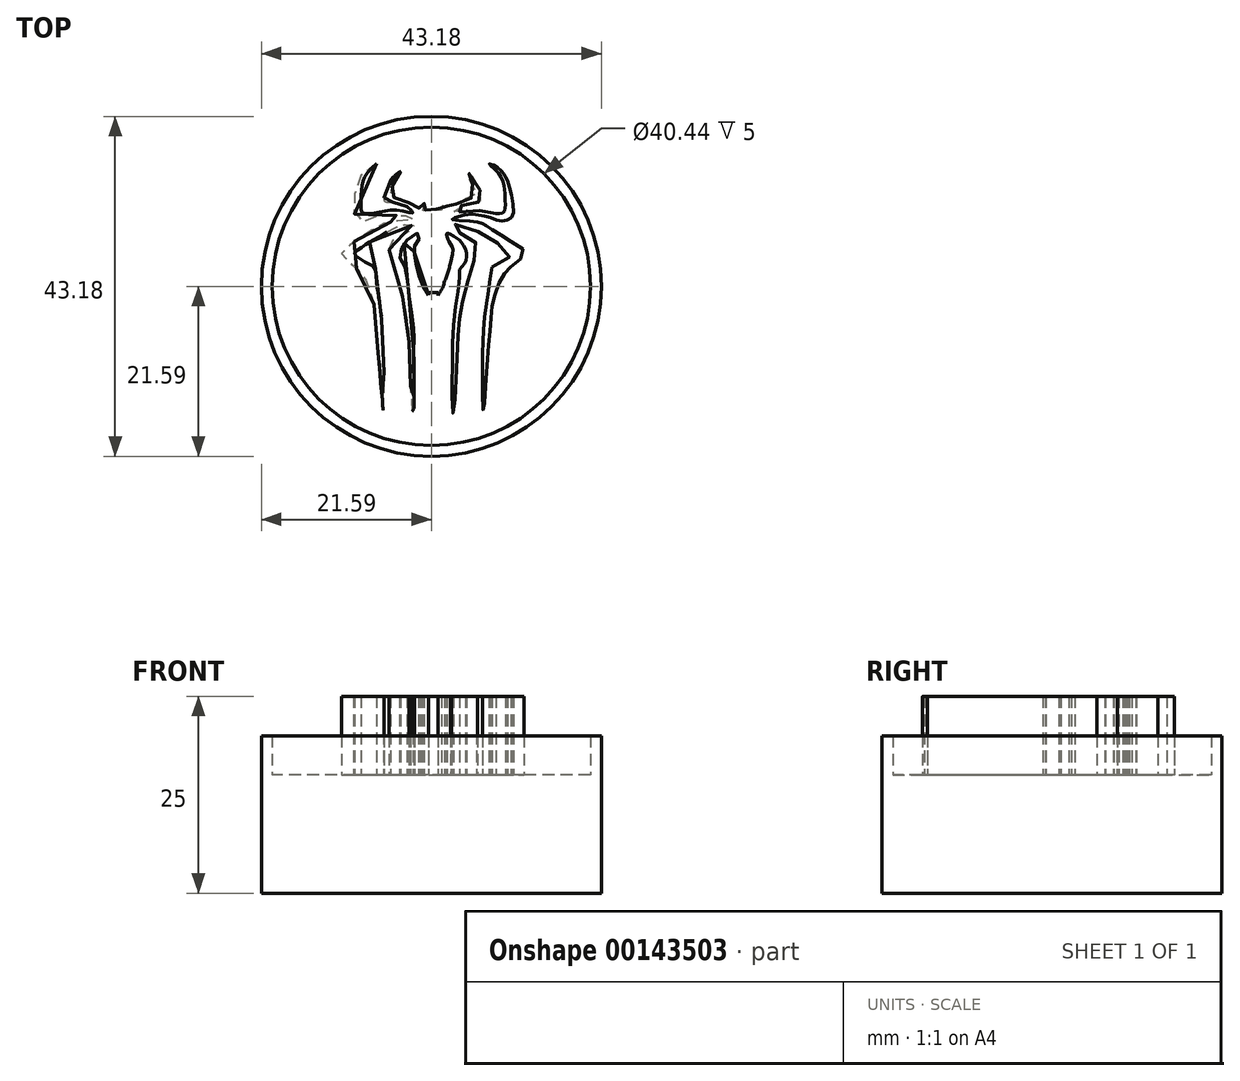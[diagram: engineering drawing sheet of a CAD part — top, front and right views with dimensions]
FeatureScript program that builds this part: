
annotation { "Feature Type Name" : "Feature", "Feature Type Description" : "" }
export const myFeature = defineFeature(function(context is Context, id is Id, definition is map)
    precondition{}
    {
        {
            var Q0;
            Q0=qCreatedBy(makeId("Top.planeOp"),FACE);
            var sketch = newSketch(context, id + "F0", { "sketchPlane" : qUnion([Q0])});
            skCircle(sketch, "E0", {"center": v(0, 0) * mm, "radius": 21.6 * mm});
            skCircle(sketch, "E1", {"center": v(0, 0) * mm, "radius": 20.22 * mm});
            skSolve(sketch);
        }
        {
            var Q0;
            Q0=makeQuery(id+"F0.imprint","IMPRINT",FACE,{"disambiguationData":[TD([[makeQuery(id+"F0.imprint","IMPRINT",EDGE,{"derivedFrom":sQuery(id+"F0.wireOp",EDGE,"E0")}),1.0]])]});
            extrude(context, id + "F1", {"entities" : qUnion([Q0]), "depth" : 20 * mm});
        }
        {
            var Q0;
            Q0=makeQuery(id+"F0.imprint","IMPRINT",FACE,{"disambiguationData":[TD([[makeQuery(id+"F0.imprint","IMPRINT",EDGE,{"derivedFrom":sQuery(id+"F0.wireOp",EDGE,"E1")}),1.0]])]});
            extrude(context, id + "F2", {"entities" : qUnion([Q0]), "operationType" : NewBodyOperationType.ADD, "depth" : 15 * mm});
        }
        {
            var Q0;
            Q0=makeQuery(id+"F2.opExtrude","CAP_FACE",FACE,{"disambiguationData":[OSD([sQuery(id+"F0.wireOp",EDGE,"E1")])],"isStart":false});
            var sketch = newSketch(context, id + "F3", { "sketchPlane" : qUnion([Q0])});
            skPoint(sketch, "E2", {"position": v(-8.55, 14.56) * mm});
            skPoint(sketch, "E3", {"position": v(-9.43, 12.92) * mm});
            skPoint(sketch, "E4", {"position": v(-9.83, 11.06) * mm});
            skPoint(sketch, "E5", {"position": v(-9.83, 9.64) * mm});
            skPoint(sketch, "E6", {"position": v(-9.48, 8.54) * mm});
            skPoint(sketch, "E7", {"position": v(-8.32, 8.54) * mm});
            skPoint(sketch, "E8", {"position": v(-7.4, 8.76) * mm});
            skPoint(sketch, "E9", {"position": v(-6.24, 9.02) * mm});
            skPoint(sketch, "E10", {"position": v(-5.18, 9.02) * mm});
            skPoint(sketch, "E11", {"position": v(-4.25, 9.02) * mm});
            skPoint(sketch, "E12", {"position": v(-3.36, 9.02) * mm});
            skPoint(sketch, "E13", {"position": v(-2.57, 8.67) * mm});
            skPoint(sketch, "E14", {"position": v(-2.18, 8.51) * mm});
            skPoint(sketch, "E15", {"position": v(-3.33, 8.51) * mm});
            skPoint(sketch, "E16", {"position": v(-4.3, 8.3) * mm});
            skPoint(sketch, "E17", {"position": v(-5.35, 8.12) * mm});
            skPoint(sketch, "E18", {"position": v(-6.07, 7.91) * mm});
            skPoint(sketch, "E19", {"position": v(-6.95, 7.47) * mm});
            skPoint(sketch, "E20", {"position": v(-7.67, 7.02) * mm});
            skPoint(sketch, "E21", {"position": v(-8.38, 6.6) * mm});
            skPoint(sketch, "E22", {"position": v(-8.94, 6.22) * mm});
            skPoint(sketch, "E23", {"position": v(-9.8, 5.65) * mm});
            skPoint(sketch, "E24", {"position": v(-10.71, 5.04) * mm});
            skPoint(sketch, "E25", {"position": v(-11.32, 4.59) * mm});
            skPoint(sketch, "E26", {"position": v(-11.32, 3.97) * mm});
            skPoint(sketch, "E27", {"position": v(-10.98, 3.63) * mm});
            skPoint(sketch, "E28", {"position": v(-10.51, 3.17) * mm});
            skPoint(sketch, "E29", {"position": v(-9.87, 2.64) * mm});
            skPoint(sketch, "E30", {"position": v(-9.23, 2.02) * mm});
            skPoint(sketch, "E31", {"position": v(-8.6, 1.38) * mm});
            skPoint(sketch, "E32", {"position": v(-8.23, 0.62) * mm});
            skPoint(sketch, "E33", {"position": v(-7.97, 0) * mm});
            skPoint(sketch, "E34", {"position": v(-7.66, -1.02) * mm});
            skPoint(sketch, "E35", {"position": v(-7.5, -1.48) * mm});
            skPoint(sketch, "E36", {"position": v(-7.26, -2.43) * mm});
            skPoint(sketch, "E37", {"position": v(-7.1, -3.32) * mm});
            skPoint(sketch, "E38", {"position": v(-7.08, -4.27) * mm});
            skPoint(sketch, "E39", {"position": v(-7.04, -4.98) * mm});
            skPoint(sketch, "E40", {"position": v(-6.95, -5.8) * mm});
            skPoint(sketch, "E41", {"position": v(-6.9, -6.93) * mm});
            skPoint(sketch, "E42", {"position": v(-6.8, -7.9) * mm});
            skPoint(sketch, "E43", {"position": v(-6.67, -9.14) * mm});
            skPoint(sketch, "E44", {"position": v(-6.57, -10.22) * mm});
            skPoint(sketch, "E45", {"position": v(-6.5, -11.18) * mm});
            skPoint(sketch, "E46", {"position": v(-6.4, -12.61) * mm});
            skPoint(sketch, "E47", {"position": v(-6.27, -13.83) * mm});
            skPoint(sketch, "E48", {"position": v(-6.17, -15.03) * mm});
            skPoint(sketch, "E49", {"position": v(-6.13, -15.83) * mm});
            skPoint(sketch, "E50", {"position": v(-6.03, -14.04) * mm});
            skPoint(sketch, "E51", {"position": v(-6.01, -12.26) * mm});
            skPoint(sketch, "E52", {"position": v(-6.03, -10.64) * mm});
            skPoint(sketch, "E53", {"position": v(-6.03, -8.76) * mm});
            skPoint(sketch, "E54", {"position": v(-6.03, -7.36) * mm});
            skPoint(sketch, "E55", {"position": v(-6.13, -5.97) * mm});
            skPoint(sketch, "E56", {"position": v(-6.2, -4.96) * mm});
            skPoint(sketch, "E57", {"position": v(-6.34, -3.93) * mm});
            skPoint(sketch, "E58", {"position": v(-6.5, -2.66) * mm});
            skPoint(sketch, "E59", {"position": v(-6.67, -1.54) * mm});
            skPoint(sketch, "E60", {"position": v(-6.8, -0.48) * mm});
            skPoint(sketch, "E61", {"position": v(-7, 0.83) * mm});
            skPoint(sketch, "E62", {"position": v(-7.23, 2.43) * mm});
            skPoint(sketch, "E63", {"position": v(-8.05, 2.9) * mm});
            skPoint(sketch, "E64", {"position": v(-9.08, 3.53) * mm});
            skPoint(sketch, "E65", {"position": v(-9.76, 4.14) * mm});
            skPoint(sketch, "E66", {"position": v(-9.1, 4.78) * mm});
            skPoint(sketch, "E67", {"position": v(-8.22, 5.39) * mm});
            skPoint(sketch, "E68", {"position": v(-7.16, 6.02) * mm});
            skPoint(sketch, "E69", {"position": v(-6.08, 6.63) * mm});
            skPoint(sketch, "E70", {"position": v(-5.26, 7.12) * mm});
            skPoint(sketch, "E71", {"position": v(-4.4, 7.57) * mm});
            skPoint(sketch, "E72", {"position": v(-3.36, 7.83) * mm});
            skPoint(sketch, "E73", {"position": v(-2.42, 7.73) * mm});
            skPoint(sketch, "E74", {"position": v(-2.12, 7.69) * mm});
            skPoint(sketch, "E75", {"position": v(-2.77, 7.05) * mm});
            skPoint(sketch, "E76", {"position": v(-3.71, 6.4) * mm});
            skPoint(sketch, "E77", {"position": v(-4.32, 6.16) * mm});
            skPoint(sketch, "E78", {"position": v(-5.05, 5.72) * mm});
            skPoint(sketch, "E79", {"position": v(-5.33, 4.94) * mm});
            skPoint(sketch, "E80", {"position": v(-5.28, 3.96) * mm});
            skPoint(sketch, "E81", {"position": v(-4.77, 2.6) * mm});
            skPoint(sketch, "E82", {"position": v(-4.37, 1.4) * mm});
            skPoint(sketch, "E83", {"position": v(-4.09, 0.2) * mm});
            skPoint(sketch, "E84", {"position": v(-3.76, -0.76) * mm});
            skPoint(sketch, "E85", {"position": v(-3.55, -1.89) * mm});
            skPoint(sketch, "E86", {"position": v(-3.31, -3.13) * mm});
            skPoint(sketch, "E87", {"position": v(-3.1, -4.4) * mm});
            skPoint(sketch, "E88", {"position": v(-2.98, -5.08) * mm});
            skPoint(sketch, "E89", {"position": v(-2.91, -5.9) * mm});
            skPoint(sketch, "E90", {"position": v(-2.87, -6.96) * mm});
            skPoint(sketch, "E91", {"position": v(-2.82, -8.22) * mm});
            skPoint(sketch, "E92", {"position": v(-2.82, -9.33) * mm});
            skPoint(sketch, "E93", {"position": v(-2.75, -10.26) * mm});
            skPoint(sketch, "E94", {"position": v(-2.7, -11.16) * mm});
            skPoint(sketch, "E95", {"position": v(-2.65, -11.88) * mm});
            skPoint(sketch, "E96", {"position": v(-2.65, -12.78) * mm});
            skPoint(sketch, "E97", {"position": v(-2.56, -13.97) * mm});
            skPoint(sketch, "E98", {"position": v(-2.5, -14.7) * mm});
            skPoint(sketch, "E99", {"position": v(-2.44, -15.76) * mm});
            skPoint(sketch, "E100", {"position": v(-2.33, -16.22) * mm});
            skPoint(sketch, "E101", {"position": v(-2.2, -15.03) * mm});
            skPoint(sketch, "E102", {"position": v(-2.2, -13.6) * mm});
            skPoint(sketch, "E103", {"position": v(-2.19, -12.4) * mm});
            skPoint(sketch, "E104", {"position": v(-2.16, -11.16) * mm});
            skPoint(sketch, "E105", {"position": v(-2.2, -10.36) * mm});
            skPoint(sketch, "E106", {"position": v(-2.23, -9.42) * mm});
            skPoint(sketch, "E107", {"position": v(-2.26, -8.41) * mm});
            skPoint(sketch, "E108", {"position": v(2.77, -16.44) * mm});
            skPoint(sketch, "E109", {"position": v(6.6, -15.83) * mm});
            skPoint(sketch, "E110", {"position": v(2.72, -15.43) * mm});
            skPoint(sketch, "E111", {"position": v(2.65, -14.42) * mm});
            skPoint(sketch, "E112", {"position": v(2.6, -13.46) * mm});
            skPoint(sketch, "E113", {"position": v(2.6, -12.45) * mm});
            skPoint(sketch, "E114", {"position": v(2.62, -11.72) * mm});
            skPoint(sketch, "E115", {"position": v(2.67, -10.83) * mm});
            skPoint(sketch, "E116", {"position": v(2.7, -8.83) * mm});
            skPoint(sketch, "E117", {"position": v(2.67, -6.8) * mm});
            skPoint(sketch, "E118", {"position": v(2.77, -5.38) * mm});
            skPoint(sketch, "E119", {"position": v(3.4, -6.65) * mm});
            skPoint(sketch, "E120", {"position": v(3.28, -8.95) * mm});
            skPoint(sketch, "E121", {"position": v(3.23, -10.66) * mm});
            skPoint(sketch, "E122", {"position": v(3.07, -12.94) * mm});
            skPoint(sketch, "E123", {"position": v(3, -14.37) * mm});
            skPoint(sketch, "E124", {"position": v(-2.2, -6.82) * mm});
            skPoint(sketch, "E125", {"position": v(-2.2, -5.97) * mm});
            skPoint(sketch, "E126", {"position": v(-2.37, -4.42) * mm});
            skPoint(sketch, "E127", {"position": v(-2.7, -1.89) * mm});
            skPoint(sketch, "E128", {"position": v(-3, 0.2) * mm});
            skPoint(sketch, "E129", {"position": v(-3.17, 2.19) * mm});
            skPoint(sketch, "E130", {"position": v(-3.82, 3.02) * mm});
            skPoint(sketch, "E131", {"position": v(-4.01, 3.96) * mm});
            skPoint(sketch, "E132", {"position": v(-3.78, 4.85) * mm});
            skPoint(sketch, "E133", {"position": v(-3.33, 5.65) * mm});
            skPoint(sketch, "E134", {"position": v(-2.58, 6.28) * mm});
            skPoint(sketch, "E135", {"position": v(-1.52, 6.77) * mm});
            skPoint(sketch, "E136", {"position": v(-1.52, 6.11) * mm});
            skPoint(sketch, "E137", {"position": v(-1.76, 5.74) * mm});
            skPoint(sketch, "E138", {"position": v(-2.11, 5.13) * mm});
            skPoint(sketch, "E139", {"position": v(-2.25, 4.8) * mm});
            skPoint(sketch, "E140", {"position": v(-2.09, 3.72) * mm});
            skPoint(sketch, "E141", {"position": v(-1.88, 2.5) * mm});
            skPoint(sketch, "E142", {"position": v(-1.67, 1.66) * mm});
            skPoint(sketch, "E143", {"position": v(-1.27, 0.65) * mm});
            skPoint(sketch, "E144", {"position": v(-0.84, -0.36) * mm});
            skPoint(sketch, "E145", {"position": v(-0.37, -1.14) * mm});
            skPoint(sketch, "E146", {"position": v(0.82, -1.16) * mm});
            skPoint(sketch, "E147", {"position": v(0.82, -0.8) * mm});
            skPoint(sketch, "E148", {"position": v(-0.37, -0.76) * mm});
            skPoint(sketch, "E149", {"position": v(1.36, -0.3) * mm});
            skPoint(sketch, "E150", {"position": v(1.71, 0.7) * mm});
            skPoint(sketch, "E151", {"position": v(2.14, 1.82) * mm});
            skPoint(sketch, "E152", {"position": v(2.42, 2.92) * mm});
            skPoint(sketch, "E153", {"position": v(2.72, 4.82) * mm});
            skPoint(sketch, "E154", {"position": v(2.28, 5.6) * mm});
            skPoint(sketch, "E155", {"position": v(2.04, 6.18) * mm});
            skPoint(sketch, "E156", {"position": v(1.93, 6.72) * mm});
            skPoint(sketch, "E157", {"position": v(2.74, 6.44) * mm});
            skPoint(sketch, "E158", {"position": v(3.7, 5.72) * mm});
            skPoint(sketch, "E159", {"position": v(4.37, 4.58) * mm});
            skPoint(sketch, "E160", {"position": v(4.39, 3.23) * mm});
            skPoint(sketch, "E161", {"position": v(3.57, 1.13) * mm});
            skPoint(sketch, "E162", {"position": v(3.48, 0.33) * mm});
            skPoint(sketch, "E163", {"position": v(3.37, -0.6) * mm});
            skPoint(sketch, "E164", {"position": v(3.26, -1.37) * mm});
            skPoint(sketch, "E165", {"position": v(3.1, -2.46) * mm});
            skPoint(sketch, "E166", {"position": v(4.09, -1.52) * mm});
            skPoint(sketch, "E167", {"position": v(3.8, -2.78) * mm});
            skPoint(sketch, "E168", {"position": v(3.6, -4.08) * mm});
            skPoint(sketch, "E169", {"position": v(3.46, -5.07) * mm});
            skPoint(sketch, "E170", {"position": v(2.85, -4.07) * mm});
            skPoint(sketch, "E171", {"position": v(7.2, -1) * mm});
            skPoint(sketch, "E172", {"position": v(7.03, -2.16) * mm});
            skPoint(sketch, "E173", {"position": v(6.68, -4.7) * mm});
            skPoint(sketch, "E174", {"position": v(6.61, -6.66) * mm});
            skPoint(sketch, "E175", {"position": v(6.5, -8.52) * mm});
            skPoint(sketch, "E176", {"position": v(7.26, -7.5) * mm});
            skPoint(sketch, "E177", {"position": v(7.51, -4.95) * mm});
            skPoint(sketch, "E178", {"position": v(7.64, -2.94) * mm});
            skPoint(sketch, "E179", {"position": v(8.06, -1.14) * mm});
            skPoint(sketch, "E180", {"position": v(8.79, 0.76) * mm});
            skPoint(sketch, "E181", {"position": v(7.45, 0.9) * mm});
            skPoint(sketch, "E182", {"position": v(6.49, -10.83) * mm});
            skPoint(sketch, "E183", {"position": v(6.48, -12.85) * mm});
            skPoint(sketch, "E184", {"position": v(7, -11.17) * mm});
            skPoint(sketch, "E185", {"position": v(4.61, 0.5) * mm});
            skPoint(sketch, "E186", {"position": v(5.09, 2.37) * mm});
            skPoint(sketch, "E187", {"position": v(5.74, 4.09) * mm});
            skPoint(sketch, "E188", {"position": v(5.7, 5.47) * mm});
            skPoint(sketch, "E189", {"position": v(4.44, 6.21) * mm});
            skPoint(sketch, "E190", {"position": v(3.25, 7.01) * mm});
            skPoint(sketch, "E191", {"position": v(2.52, 7.66) * mm});
            skPoint(sketch, "E192", {"position": v(4.44, 7.78) * mm});
            skPoint(sketch, "E193", {"position": v(6.3, 6.69) * mm});
            skPoint(sketch, "E194", {"position": v(8.16, 5.65) * mm});
            skPoint(sketch, "E195", {"position": v(10.17, 4.2) * mm});
            skPoint(sketch, "E196", {"position": v(9.08, 3.23) * mm});
            skPoint(sketch, "E197", {"position": v(7.69, 2.46) * mm});
            skPoint(sketch, "E198", {"position": v(9.5, 1.9) * mm});
            skPoint(sketch, "E199", {"position": v(10.44, 2.73) * mm});
            skPoint(sketch, "E200", {"position": v(11.77, 4.32) * mm});
            skPoint(sketch, "E201", {"position": v(10.11, 5.71) * mm});
            skPoint(sketch, "E202", {"position": v(7.04, 7.63) * mm});
            skPoint(sketch, "E203", {"position": v(6.5, 7.96) * mm});
            skPoint(sketch, "E204", {"position": v(5.03, 8.28) * mm});
            skPoint(sketch, "E205", {"position": v(2.6, 8.52) * mm});
            skPoint(sketch, "E206", {"position": v(4.56, 9.11) * mm});
            skPoint(sketch, "E207", {"position": v(6.1, 9.05) * mm});
            skPoint(sketch, "E208", {"position": v(7.52, 8.72) * mm});
            skPoint(sketch, "E209", {"position": v(8.72, 8.32) * mm});
            skPoint(sketch, "E210", {"position": v(9.75, 8.49) * mm});
            skPoint(sketch, "E211", {"position": v(10.34, 8.98) * mm});
            skPoint(sketch, "E212", {"position": v(10.25, 11.4) * mm});
            skPoint(sketch, "E213", {"position": v(9.65, 13.43) * mm});
            skPoint(sketch, "E214", {"position": v(8.69, 14.86) * mm});
            skPoint(sketch, "E215", {"position": v(7.36, 15.57) * mm});
            skPoint(sketch, "E216", {"position": v(8.59, 14.33) * mm});
            skPoint(sketch, "E217", {"position": v(9.32, 12.37) * mm});
            skPoint(sketch, "E218", {"position": v(9.38, 10.74) * mm});
            skPoint(sketch, "E219", {"position": v(9.22, 9.45) * mm});
            skPoint(sketch, "E220", {"position": v(8.19, 9.25) * mm});
            skPoint(sketch, "E221", {"position": v(7, 9.42) * mm});
            skPoint(sketch, "E222", {"position": v(5.86, 9.65) * mm});
            skPoint(sketch, "E223", {"position": v(4.2, 9.55) * mm});
            skPoint(sketch, "E224", {"position": v(2.84, 9.42) * mm});
            skPoint(sketch, "E225", {"position": v(3.74, 10.21) * mm});
            skPoint(sketch, "E226", {"position": v(5.17, 10.7) * mm});
            skPoint(sketch, "E227", {"position": v(6.26, 10.74) * mm});
            skPoint(sketch, "E228", {"position": v(6.53, 11.04) * mm});
            skPoint(sketch, "E229", {"position": v(6.06, 12.44) * mm});
            skPoint(sketch, "E230", {"position": v(5.27, 13.9) * mm});
            skPoint(sketch, "E231", {"position": v(4.34, 14.6) * mm});
            skPoint(sketch, "E232", {"position": v(5.4, 12.73) * mm});
            skPoint(sketch, "E233", {"position": v(5.6, 11.37) * mm});
            skPoint(sketch, "E234", {"position": v(4.57, 11.14) * mm});
            skPoint(sketch, "E235", {"position": v(3.5, 10.74) * mm});
            skPoint(sketch, "E236", {"position": v(2.51, 10.01) * mm});
            skPoint(sketch, "E237", {"position": v(2.01, 9.85) * mm});
            skPoint(sketch, "E238", {"position": v(1.92, 10.38) * mm});
            skPoint(sketch, "E239", {"position": v(1.29, 10.66) * mm});
            skPoint(sketch, "E240", {"position": v(1.62, 10.11) * mm});
            skPoint(sketch, "E241", {"position": v(1.59, 9.77) * mm});
            skPoint(sketch, "E242", {"position": v(1.43, 9.61) * mm});
            skPoint(sketch, "E243", {"position": v(0.82, 9.86) * mm});
            skPoint(sketch, "E244", {"position": v(0.22, 9.55) * mm});
            skPoint(sketch, "E245", {"position": v(-0.4, 9.85) * mm});
            skPoint(sketch, "E246", {"position": v(-1, 9.61) * mm});
            skPoint(sketch, "E247", {"position": v(-1.19, 9.91) * mm});
            skPoint(sketch, "E248", {"position": v(-1.06, 10.3) * mm});
            skPoint(sketch, "E249", {"position": v(-0.9, 10.63) * mm});
            skPoint(sketch, "E250", {"position": v(-1.3, 10.5) * mm});
            skPoint(sketch, "E251", {"position": v(-1.62, 10.11) * mm});
            skPoint(sketch, "E252", {"position": v(-1.6, 9.85) * mm});
            skPoint(sketch, "E253", {"position": v(-2.12, 10) * mm});
            skPoint(sketch, "E254", {"position": v(-2.9, 10.66) * mm});
            skPoint(sketch, "E255", {"position": v(-3.77, 11.09) * mm});
            skPoint(sketch, "E256", {"position": v(-4.83, 11.26) * mm});
            skPoint(sketch, "E257", {"position": v(-5.18, 11.4) * mm});
            skPoint(sketch, "E258", {"position": v(-5, 12.6) * mm});
            skPoint(sketch, "E259", {"position": v(-4.55, 13.7) * mm});
            skPoint(sketch, "E260", {"position": v(-3.93, 14.58) * mm});
            skPoint(sketch, "E261", {"position": v(-4.83, 13.89) * mm});
            skPoint(sketch, "E262", {"position": v(-5.35, 13.07) * mm});
            skPoint(sketch, "E263", {"position": v(-5.82, 11.82) * mm});
            skPoint(sketch, "E264", {"position": v(-6.04, 11.04) * mm});
            skPoint(sketch, "E265", {"position": v(-5.82, 10.76) * mm});
            skPoint(sketch, "E266", {"position": v(-4.98, 10.7) * mm});
            skPoint(sketch, "E267", {"position": v(-4.08, 10.54) * mm});
            skPoint(sketch, "E268", {"position": v(-3.06, 10.13) * mm});
            skPoint(sketch, "E269", {"position": v(-2.36, 9.35) * mm});
            skPoint(sketch, "E270", {"position": v(-3.52, 9.55) * mm});
            skPoint(sketch, "E271", {"position": v(-5.66, 9.63) * mm});
            skPoint(sketch, "E272", {"position": v(-7.23, 9.3) * mm});
            skPoint(sketch, "E273", {"position": v(-8.45, 9.24) * mm});
            skPoint(sketch, "E274", {"position": v(-8.83, 9.43) * mm});
            skPoint(sketch, "E275", {"position": v(-8.92, 10.43) * mm});
            skPoint(sketch, "E276", {"position": v(-8.94, 11.8) * mm});
            skPoint(sketch, "E277", {"position": v(-8.73, 13.01) * mm});
            skPoint(sketch, "E278", {"position": v(-8.36, 14.1) * mm});
            skPoint(sketch, "E279", {"position": v(-6.98, 15.57) * mm});
            skFitSpline(sketch, "E280", {"points": [v(-6.98, 15.57) * mm, v(-8.55, 14.56) * mm, v(-9.43, 12.92) * mm, v(-9.83, 11.06) * mm, v(-9.83, 9.64) * mm, v(-9.48, 8.54) * mm, v(-8.55, 8.26) * mm, v(-7.4, 8.76) * mm, v(-6.24, 9.02) * mm, v(-5.18, 9.02) * mm, v(-4.25, 9.02) * mm, v(-3.36, 9.02) * mm, v(-2.57, 8.67) * mm, v(-2.18, 8.51) * mm, v(-3.33, 8.51) * mm, v(-4.3, 8.3) * mm, v(-5.35, 8.12) * mm, v(-6.07, 7.91) * mm, v(-6.95, 7.47) * mm, v(-7.67, 7.02) * mm, v(-8.38, 6.6) * mm, v(-8.94, 6.22) * mm, v(-9.8, 5.65) * mm, v(-10.71, 5.04) * mm, v(-11.32, 4.59) * mm, v(-11.32, 3.97) * mm, v(-10.98, 3.63) * mm, v(-10.51, 3.17) * mm, v(-9.87, 2.64) * mm, v(-9.23, 2.02) * mm, v(-8.6, 1.38) * mm, v(-8.23, 0.62) * mm, v(-7.97, 0) * mm, v(-7.66, -1.02) * mm, v(-7.5, -1.48) * mm, v(-7.26, -2.43) * mm, v(-7.1, -3.32) * mm, v(-7.08, -4.27) * mm, v(-7.04, -4.98) * mm, v(-6.95, -5.8) * mm, v(-6.9, -6.93) * mm, v(-6.8, -7.9) * mm, v(-6.67, -9.14) * mm, v(-6.57, -10.22) * mm, v(-6.5, -11.18) * mm, v(-6.4, -12.61) * mm, v(-6.27, -13.83) * mm, v(-6.17, -15.03) * mm, v(-6.13, -15.83) * mm, v(-6.03, -14.04) * mm, v(-6.01, -12.26) * mm, v(-6.03, -10.64) * mm, v(-6.03, -8.76) * mm, v(-6.03, -7.36) * mm, v(-6.13, -5.97) * mm, v(-6.2, -4.96) * mm, v(-6.34, -3.93) * mm, v(-6.5, -2.66) * mm, v(-6.67, -1.54) * mm, v(-6.8, -0.48) * mm, v(-7, 0.83) * mm, v(-7.23, 2.43) * mm, v(-8.05, 2.9) * mm, v(-9.08, 3.53) * mm, v(-9.76, 4.14) * mm, v(-9.1, 4.78) * mm, v(-8.22, 5.39) * mm, v(-7.16, 6.02) * mm, v(-6.08, 6.63) * mm, v(-5.26, 7.12) * mm, v(-4.4, 7.57) * mm, v(-3.36, 7.83) * mm, v(-2.42, 7.73) * mm, v(-2.12, 7.69) * mm, v(-2.77, 7.05) * mm, v(-3.71, 6.4) * mm, v(-4.32, 6.16) * mm, v(-5.05, 5.72) * mm, v(-5.33, 4.94) * mm, v(-5.28, 3.96) * mm, v(-4.77, 2.6) * mm, v(-4.37, 1.4) * mm, v(-4.09, 0.2) * mm, v(-3.76, -0.76) * mm, v(-3.55, -1.89) * mm, v(-3.31, -3.13) * mm, v(-3.1, -4.4) * mm, v(-2.98, -5.08) * mm, v(-2.91, -5.9) * mm, v(-2.87, -6.96) * mm, v(-2.82, -8.22) * mm, v(-2.82, -9.33) * mm, v(-2.75, -10.26) * mm, v(-2.7, -11.16) * mm, v(-2.65, -11.88) * mm, v(-2.65, -12.78) * mm, v(-2.56, -13.97) * mm, v(-2.5, -14.7) * mm, v(-2.44, -15.76) * mm, v(-2.33, -16.22) * mm, v(-2.2, -15.03) * mm, v(-2.2, -13.6) * mm, v(-2.19, -12.4) * mm, v(-2.16, -11.16) * mm, v(-2.2, -10.36) * mm, v(-2.23, -9.42) * mm, v(-2.26, -8.41) * mm, v(-2.2, -6.82) * mm, v(-2.2, -5.97) * mm, v(-2.37, -4.42) * mm, v(-2.7, -1.89) * mm, v(-3, 0.2) * mm, v(-3.17, 2.19) * mm, v(-3.82, 3.02) * mm, v(-4.01, 3.96) * mm, v(-3.78, 4.85) * mm, v(-3.33, 5.65) * mm, v(-2.58, 6.28) * mm, v(-1.52, 6.77) * mm, v(-1.52, 6.11) * mm, v(-1.76, 5.74) * mm, v(-2.11, 5.13) * mm, v(-2.25, 4.8) * mm, v(-2.09, 3.72) * mm, v(-1.88, 2.5) * mm, v(-1.67, 1.66) * mm, v(-1.27, 0.65) * mm, v(-0.84, -0.36) * mm, v(-0.37, -1.14) * mm, v(-0.37, -0.76) * mm], "startDerivative": vector(-165.29, -82.54) * mm, "endDerivative": vector(-14.41, 119.09) * mm});
            skLineSegment(sketch, "E281", {"start": v(-0.37, -0.76) * mm, "end": v(0.82, -0.8) * mm});
            skLineSegment(sketch, "E282", {"start": v(0.82, -0.8) * mm, "end": v(0.82, -1.16) * mm});
            skFitSpline(sketch, "E283", {"points": [v(0.82, -1.16) * mm, v(1.36, -0.3) * mm, v(1.71, 0.7) * mm, v(2.14, 1.82) * mm, v(2.42, 2.92) * mm], "startDerivative": vector(2.47, 3.5) * mm, "endDerivative": vector(0.95, 4.34) * mm});
            skLineSegment(sketch, "E284", {"start": v(-0.37, -0.76) * mm, "end": v(-0.37, -1.14) * mm});
            skPoint(sketch, "E285", {"position": v(3.58, 2.15) * mm});
            skLineSegment(sketch, "E286", {"start": v(3.58, 2.15) * mm, "end": v(3.57, 1.13) * mm});
            skFitSpline(sketch, "E287", {"points": [v(3.57, 1.13) * mm, v(3.48, 0.33) * mm, v(3.37, -0.6) * mm, v(3.26, -1.37) * mm, v(3.1, -2.46) * mm, v(2.85, -4.07) * mm, v(2.77, -5.38) * mm, v(2.67, -6.8) * mm, v(2.7, -8.83) * mm, v(2.67, -10.83) * mm, v(2.62, -11.86) * mm, v(2.6, -12.45) * mm, v(2.6, -13.46) * mm, v(2.65, -14.42) * mm, v(2.72, -15.43) * mm, v(2.77, -16.44) * mm, v(3, -14.37) * mm, v(3.07, -12.94) * mm, v(3.23, -10.66) * mm, v(3.28, -8.95) * mm, v(3.4, -6.65) * mm, v(3.46, -5.07) * mm, v(3.6, -4.08) * mm, v(3.8, -2.78) * mm, v(4.09, -1.52) * mm, v(4.61, 0.5) * mm, v(5.09, 2.37) * mm, v(5.74, 4.09) * mm, v(5.7, 5.47) * mm, v(4.44, 6.21) * mm, v(3.25, 7.01) * mm, v(2.52, 7.66) * mm, v(4.44, 7.78) * mm, v(6.3, 6.69) * mm, v(8.16, 5.65) * mm, v(10.17, 4.2) * mm, v(9.08, 3.23) * mm, v(7.69, 2.46) * mm], "startDerivative": vector(-4.62, -38.54) * mm, "endDerivative": vector(-45.5, -25.42) * mm});
            skLineSegment(sketch, "E288", {"start": v(7.69, 2.46) * mm, "end": v(7.45, 0.9) * mm});
            skLineSegment(sketch, "E289", {"start": v(7.45, 0.9) * mm, "end": v(7.2, -1) * mm});
            skFitSpline(sketch, "E290", {"points": [v(2.42, 2.92) * mm, v(2.72, 4.82) * mm, v(2.28, 5.6) * mm, v(2.04, 6.18) * mm, v(1.93, 6.72) * mm, v(2.74, 6.44) * mm, v(3.7, 5.72) * mm, v(4.37, 4.58) * mm, v(4.39, 3.23) * mm, v(3.58, 2.15) * mm], "startDerivative": vector(4.28, 14.34) * mm, "endDerivative": vector(-7.97, -8.1) * mm});
            skFitSpline(sketch, "E291", {"points": [v(7.2, -1) * mm, v(7.03, -2.16) * mm, v(6.68, -4.7) * mm, v(6.61, -6.66) * mm, v(6.5, -8.52) * mm, v(6.49, -10.83) * mm, v(6.48, -12.85) * mm, v(6.6, -15.83) * mm, v(7, -11.17) * mm, v(7.26, -7.5) * mm, v(7.51, -4.95) * mm, v(7.64, -2.94) * mm, v(8.06, -1.14) * mm, v(8.79, 0.76) * mm, v(9.5, 1.9) * mm, v(10.44, 2.73) * mm, v(11.77, 4.32) * mm, v(10.11, 5.71) * mm], "startDerivative": vector(-3.2, -24.06) * mm, "endDerivative": vector(-42.6, 21.84) * mm});
            skFitSpline(sketch, "E292", {"points": [v(10.11, 5.71) * mm, v(7.04, 7.63) * mm, v(6.5, 7.96) * mm, v(5.03, 8.28) * mm, v(2.6, 8.52) * mm, v(4.56, 9.11) * mm, v(6.1, 9.05) * mm, v(7.52, 8.72) * mm, v(8.72, 8.32) * mm, v(9.75, 8.49) * mm, v(10.34, 8.98) * mm, v(10.25, 11.4) * mm, v(9.65, 13.43) * mm], "startDerivative": vector(-30.44, 18.78) * mm, "endDerivative": vector(-6.85, 19.54) * mm});
            skFitSpline(sketch, "E293", {"points": [v(9.65, 13.43) * mm, v(8.69, 14.86) * mm, v(7.36, 15.57) * mm, v(8.59, 14.33) * mm, v(9.32, 12.24) * mm, v(9.38, 10.74) * mm, v(9.22, 9.45) * mm, v(8.19, 9.25) * mm], "startDerivative": vector(-4.27, 9.87) * mm, "endDerivative": vector(-10.6, 0.36) * mm});
            skFitSpline(sketch, "E294", {"points": [v(8.19, 9.25) * mm, v(7, 9.42) * mm, v(5.86, 9.65) * mm, v(4.2, 9.55) * mm, v(2.84, 9.42) * mm, v(3.74, 10.21) * mm, v(5.17, 10.7) * mm, v(6.26, 10.74) * mm, v(6.53, 11.04) * mm, v(6.06, 12.44) * mm, v(5.27, 13.9) * mm, v(4.34, 14.6) * mm, v(5.4, 12.73) * mm, v(5.6, 11.37) * mm, v(4.57, 11.14) * mm, v(3.5, 10.74) * mm, v(2.51, 10.01) * mm, v(2.01, 9.85) * mm, v(1.92, 10.38) * mm, v(1.29, 10.66) * mm, v(1.62, 10.11) * mm, v(1.59, 9.77) * mm, v(1.43, 9.61) * mm, v(0.82, 9.86) * mm, v(0.22, 9.55) * mm, v(-0.4, 9.85) * mm, v(-1, 9.61) * mm, v(-1.19, 9.91) * mm, v(-1.06, 10.3) * mm, v(-0.9, 10.63) * mm, v(-1.3, 10.5) * mm, v(-1.62, 10.11) * mm, v(-1.6, 9.85) * mm, v(-2.12, 10) * mm, v(-2.9, 10.66) * mm, v(-3.77, 11.09) * mm, v(-4.83, 11.26) * mm, v(-5.18, 11.4) * mm, v(-5, 12.6) * mm, v(-4.55, 13.7) * mm, v(-3.93, 14.58) * mm, v(-4.83, 13.89) * mm, v(-5.35, 13.07) * mm, v(-5.82, 11.82) * mm, v(-6.04, 11.04) * mm, v(-5.82, 10.76) * mm, v(-4.98, 10.7) * mm, v(-4.08, 10.54) * mm, v(-3.06, 10.13) * mm], "startDerivative": vector(-49.12, 5.3) * mm, "endDerivative": vector(44.04, -19.04) * mm});
            skFitSpline(sketch, "E295", {"points": [v(-3.06, 10.13) * mm, v(-2.36, 9.35) * mm, v(-3.52, 9.55) * mm, v(-5.66, 9.63) * mm, v(-7.23, 9.3) * mm, v(-8.45, 9.24) * mm, v(-8.83, 9.43) * mm, v(-8.92, 10.43) * mm, v(-8.94, 11.8) * mm, v(-8.73, 13.01) * mm, v(-8.36, 14.1) * mm, v(-6.98, 15.57) * mm], "startDerivative": vector(13.76, -12.5) * mm, "endDerivative": vector(14.2, 13.02) * mm});
            skSolve(sketch);
        }
        {
            var Q0;
            Q0=makeQuery(id+"F3.imprint","IMPRINT",FACE,{"disambiguationData":[TD([[makeQuery(id+"F3.imprint","IMPRINT",EDGE,{"derivedFrom":sQuery(id+"F3.wireOp",EDGE,"E281")}),1.0]])]});
            extrude(context, id + "F4", {"entities" : qUnion([Q0]), "depth" : 10 * mm});
        }
    });
